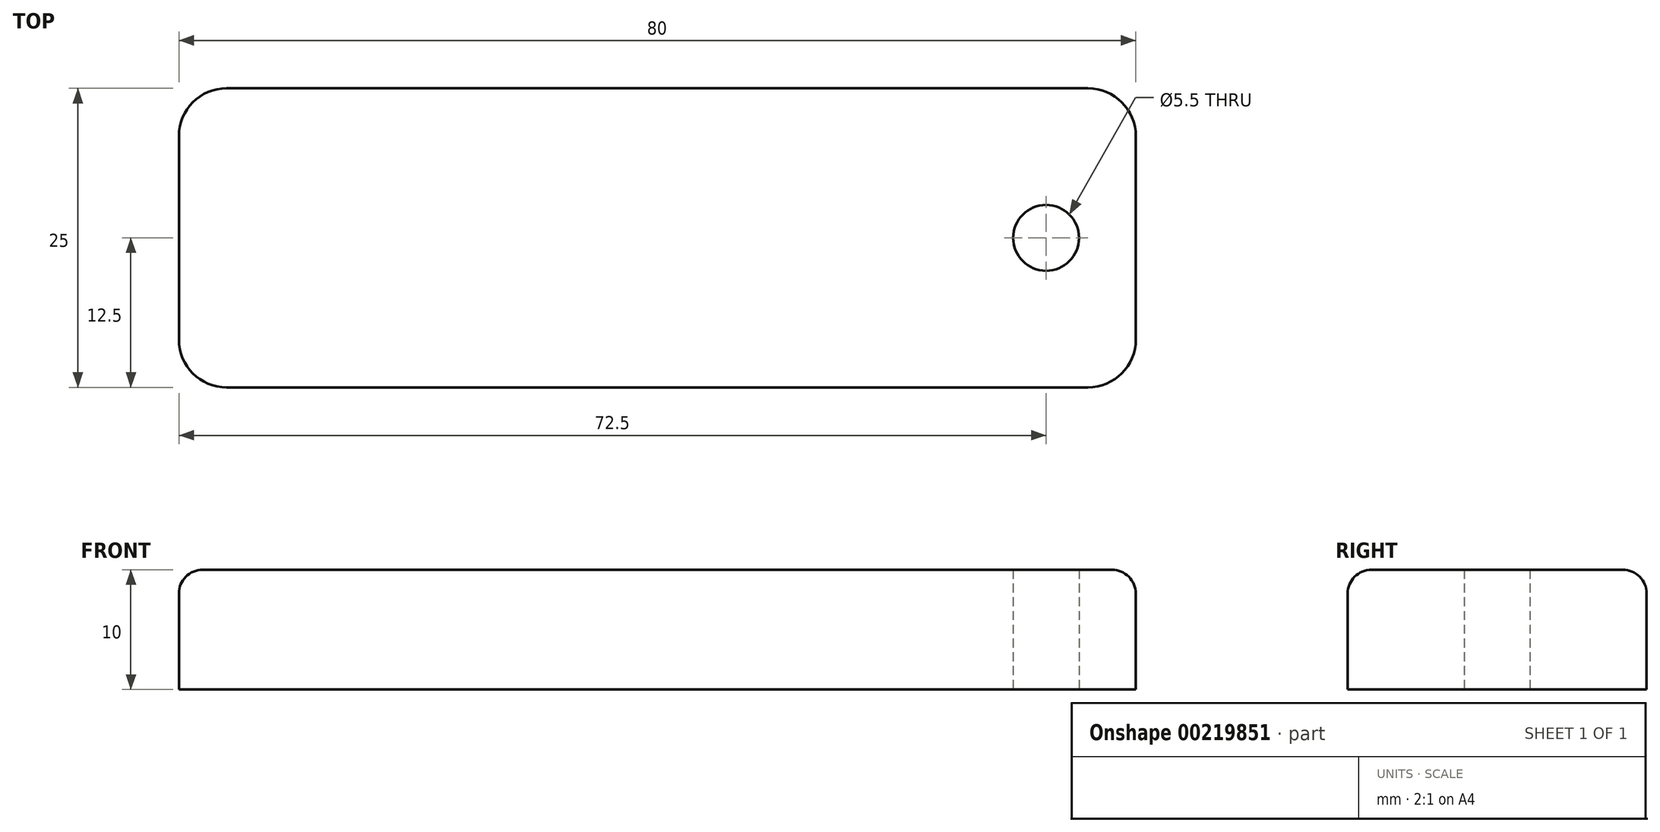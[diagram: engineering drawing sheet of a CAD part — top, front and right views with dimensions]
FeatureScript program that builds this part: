
annotation { "Feature Type Name" : "Feature", "Feature Type Description" : "" }
export const myFeature = defineFeature(function(context is Context, id is Id, definition is map)
    precondition{}
    {
        {
            var Q0;
            Q0=qCreatedBy(makeId("Top.planeOp"),FACE);
            var sketch = newSketch(context, id + "F0", { "sketchPlane" : qUnion([Q0])});
            skLineSegment(sketch, "E0.bottom", {"start": v(40, -12.5) * mm, "end": v(-40, -12.5) * mm});
            skLineSegment(sketch, "E0.top", {"start": v(40, 12.5) * mm, "end": v(-40, 12.5) * mm});
            skLineSegment(sketch, "E0.left", {"start": v(40, -12.5) * mm, "end": v(40, 12.5) * mm});
            skLineSegment(sketch, "E0.right", {"start": v(-40, -12.5) * mm, "end": v(-40, 12.5) * mm});
            skPoint(sketch, "E0.middle", {"position": v(0, 0) * mm});
            skCircle(sketch, "E1", {"center": v(32.5, 0) * mm, "radius": 2.75 * mm});
            skSolve(sketch);
        }
        {
            var Q0;
            Q0=qSketchRegion(id+"F0",true);
            extrude(context, id + "F1", {"entities" : qUnion([Q0]), "depth" : 10 * mm});
        }
        {
            var Q0;
            Q0=makeQuery(id+"F1.opExtrude","SWEPT_EDGE",EDGE,{"disambiguationData":[OSD([sQuery(id+"F0.wireOp",EDGE,"E0.bottom"),sQuery(id+"F0.wireOp",EDGE,"E0.left")])]});
            var Q1;
            Q1=makeQuery(id+"F1.opExtrude","SWEPT_EDGE",EDGE,{"disambiguationData":[OSD([sQuery(id+"F0.wireOp",EDGE,"E0.bottom"),sQuery(id+"F0.wireOp",EDGE,"E0.right")])]});
            var Q2;
            Q2=makeQuery(id+"F1.opExtrude","SWEPT_EDGE",EDGE,{"disambiguationData":[OSD([sQuery(id+"F0.wireOp",EDGE,"E0.top"),sQuery(id+"F0.wireOp",EDGE,"E0.left")])]});
            var Q3;
            Q3=makeQuery(id+"F1.opExtrude","SWEPT_EDGE",EDGE,{"disambiguationData":[OSD([sQuery(id+"F0.wireOp",EDGE,"E0.top"),sQuery(id+"F0.wireOp",EDGE,"E0.right")])]});
            fillet(context, id + "F2", {"entities" : qUnion([Q0, Q1, Q2, Q3]), "radius" : 4 * mm, "tangentPropagation" : true, "allowEdgeOverflow" : false});
        }
        {
            var Q0;
            Q0=makeQuery(id+"F1.opExtrude","CAP_EDGE",EDGE,{"disambiguationData":[OSD([sQuery(id+"F0.wireOp",EDGE,"E0.bottom")])],"isStart":false});
            fillet(context, id + "F3", {"entities" : qUnion([Q0]), "radius" : 2 * mm, "tangentPropagation" : true, "allowEdgeOverflow" : false});
        }
    });
